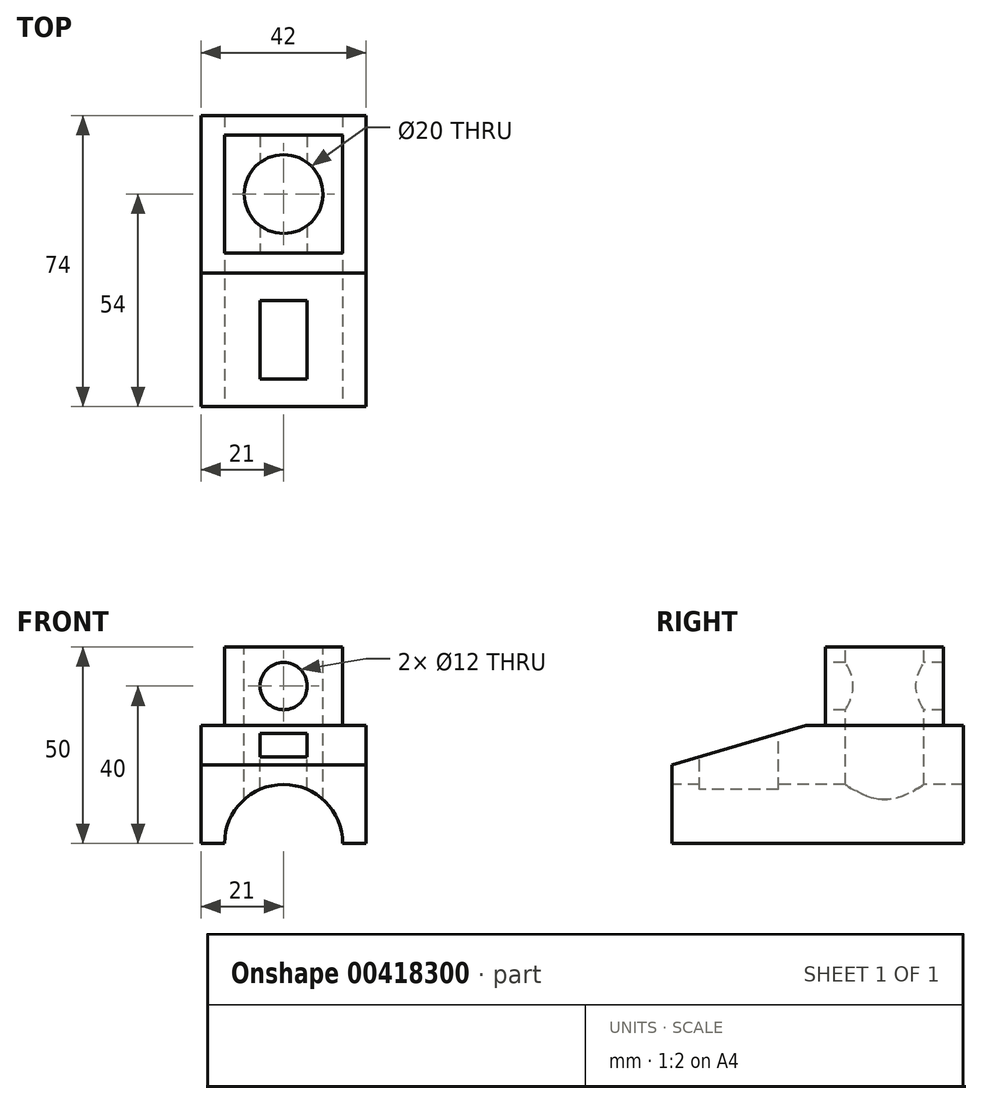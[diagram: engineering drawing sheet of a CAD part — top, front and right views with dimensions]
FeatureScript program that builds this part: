
annotation { "Feature Type Name" : "Feature", "Feature Type Description" : "" }
export const myFeature = defineFeature(function(context is Context, id is Id, definition is map)
    precondition{}
    {
        {
            var Q0;
            Q0=qCreatedBy(makeId("Right.planeOp"),FACE);
            var sketch = newSketch(context, id + "F0", { "sketchPlane" : qUnion([Q0])});
            skLineSegment(sketch, "E0.bottom", {"start": v(-37, 15) * mm, "end": v(37, 15) * mm});
            skLineSegment(sketch, "E0.top", {"start": v(-37, -15) * mm, "end": v(37, -15) * mm});
            skLineSegment(sketch, "E0.left", {"start": v(-37, 15) * mm, "end": v(-37, -15) * mm});
            skLineSegment(sketch, "E0.right", {"start": v(37, 15) * mm, "end": v(37, -15) * mm});
            skPoint(sketch, "E0.middle", {"position": v(0, 0) * mm});
            skSolve(sketch);
        }
        {
            var Q0;
            Q0 = qSketchRegion(id + "F0", true);
            extrude(context, id + "F1", {"entities" : qUnion([Q0]), "endBound" : BoundingType.SYMMETRIC, "depth" : 42 * mm});
        }
        {
            var Q0;
            Q0=makeQuery(id+"F1.opExtrude","SWEPT_EDGE",EDGE,{"disambiguationData":[OSD([sQuery(id+"F0.wireOp",EDGE,"E0.bottom"),sQuery(id+"F0.wireOp",EDGE,"E0.left")])]});
            chamfer(context, id + "F2", {"entities" : qUnion([Q0]), "chamferType" : ChamferType.TWO_OFFSETS, "width1" : 10 * mm, "oppositeDirection" : false, "width2" : 34 * mm, "tangentPropagation" : true});
        }
        {
            var Q0;
            Q0=makeQuery(id+"F1.opExtrude","SWEPT_FACE",FACE,{"disambiguationData":[OSD([sQuery(id+"F0.wireOp",EDGE,"E0.bottom")])]});
            var sketch = newSketch(context, id + "F3", { "sketchPlane" : qUnion([Q0])});
            skLineSegment(sketch, "E1.bottom", {"start": v(15, 2) * mm, "end": v(-15, 2) * mm});
            skLineSegment(sketch, "E1.top", {"start": v(15, 32) * mm, "end": v(-15, 32) * mm});
            skLineSegment(sketch, "E1.left", {"start": v(15, 2) * mm, "end": v(15, 32) * mm});
            skLineSegment(sketch, "E1.right", {"start": v(-15, 2) * mm, "end": v(-15, 32) * mm});
            skPoint(sketch, "E1.middle", {"position": v(0, 17) * mm});
            skPoint(sketch, "E1.middle.positionSnap0", {"position": v(-21, 17) * mm});
            skPoint(sketch, "E1.middle.positionSnap1", {"position": v(0, 37) * mm});
            skPoint(sketch, "E1.centerSnap0", {"position": v(-21, 17) * mm});
            skPoint(sketch, "E1.centerSnap1", {"position": v(0, 37) * mm});
            skSolve(sketch);
        }
        {
            var Q0;
            Q0 = qSketchRegion(id + "F3", true);
            extrude(context, id + "F4", {"entities" : qUnion([Q0]), "operationType" : NewBodyOperationType.ADD, "depth" : 20 * mm});
        }
        {
            var Q0;
            Q0=makeQuery(id+"F4.opExtrude","CAP_FACE",FACE,{"disambiguationData":[OSD([sQuery(id+"F3.wireOp",EDGE,"E1.bottom"),sQuery(id+"F3.wireOp",EDGE,"E1.top"),sQuery(id+"F3.wireOp",EDGE,"E1.left"),sQuery(id+"F3.wireOp",EDGE,"E1.right")])],"isStart":false});
            var sketch = newSketch(context, id + "F5", { "sketchPlane" : qUnion([Q0])});
            skCircle(sketch, "E2", {"center": v(0, 17) * mm, "radius": 10 * mm});
            skPoint(sketch, "E2.centerSnap0", {"position": v(-15, 17) * mm});
            skPoint(sketch, "E2.centerSnap1", {"position": v(0, 2) * mm});
            skSolve(sketch);
        }
        {
            var Q0;
            Q0 = qSketchRegion(id + "F5", true);
            extrude(context, id + "F6", {"entities" : qUnion([Q0]), "operationType" : NewBodyOperationType.REMOVE, "endBound" : BoundingType.THROUGH_ALL, "oppositeDirection" : true, "depth" : 25 * mm});
        }
        {
            var Q0;
            Q0=makeQuery(id+"F4.opExtrude","SWEPT_FACE",FACE,{"disambiguationData":[OSD([sQuery(id+"F3.wireOp",EDGE,"E1.bottom")])]});
            var sketch = newSketch(context, id + "F7", { "sketchPlane" : qUnion([Q0])});
            skCircle(sketch, "E3", {"center": v(0, 25) * mm, "radius": 6 * mm});
            skPoint(sketch, "E3.centerSnap0", {"position": v(0, 35) * mm});
            skPoint(sketch, "E3.centerSnap1", {"position": v(-15, 25) * mm});
            skSolve(sketch);
        }
        {
            var Q0;
            Q0 = qSketchRegion(id + "F7", true);
            extrude(context, id + "F8", {"entities" : qUnion([Q0]), "operationType" : NewBodyOperationType.REMOVE, "endBound" : BoundingType.THROUGH_ALL, "oppositeDirection" : true, "depth" : 25 * mm});
        }
        {
            var Q0;
            Q0=makeQuery(id+"F1.opExtrude","SWEPT_FACE",FACE,{"disambiguationData":[OSD([sQuery(id+"F0.wireOp",EDGE,"E0.left")])]});
            var sketch = newSketch(context, id + "F9", { "sketchPlane" : qUnion([Q0])});
            skCircle(sketch, "E4", {"center": v(0, -15) * mm, "radius": 15 * mm});
            skSolve(sketch);
        }
        {
            var Q0;
            Q0=makeQuery(id+"F1.opExtrude","SWEPT_FACE",FACE,{"disambiguationData":[OSD([sQuery(id+"F0.wireOp",EDGE,"E0.bottom")])]});
            var sketch = newSketch(context, id + "F10", { "sketchPlane" : qUnion([Q0])});
            skLineSegment(sketch, "E5.bottom", {"start": v(6, -10) * mm, "end": v(-6, -10) * mm});
            skLineSegment(sketch, "E5.top", {"start": v(6, -30) * mm, "end": v(-6, -30) * mm});
            skLineSegment(sketch, "E5.left", {"start": v(6, -10) * mm, "end": v(6, -30) * mm});
            skLineSegment(sketch, "E5.right", {"start": v(-6, -10) * mm, "end": v(-6, -30) * mm});
            skSolve(sketch);
        }
        {
            var Q0;
            Q0 = qSketchRegion(id + "F10", true);
            var Q1;
            Q1=makeQuery(id+"F12.boolean.opBoolean","COPY",FACE,{"derivedFrom":makeQuery(id+"F12.opExtrude","SWEPT_FACE",FACE,{"disambiguationData":[OSD([sQuery(id+"F9.wireOp",EDGE,"E4")])]})});
            extrude(context, id + "F11", {"entities" : qUnion([Q0]), "operationType" : NewBodyOperationType.REMOVE, "endBound" : BoundingType.THROUGH_ALL, "oppositeDirection" : true, "endBoundEntityFace" : qUnion([Q1]), "depth" : 25 * mm});
        }
        {
            var Q0;
            Q0 = qSketchRegion(id + "F9", true);
            extrude(context, id + "F12", {"entities" : qUnion([Q0]), "operationType" : NewBodyOperationType.REMOVE, "endBound" : BoundingType.THROUGH_ALL, "oppositeDirection" : true, "depth" : 25 * mm});
        }
    });
